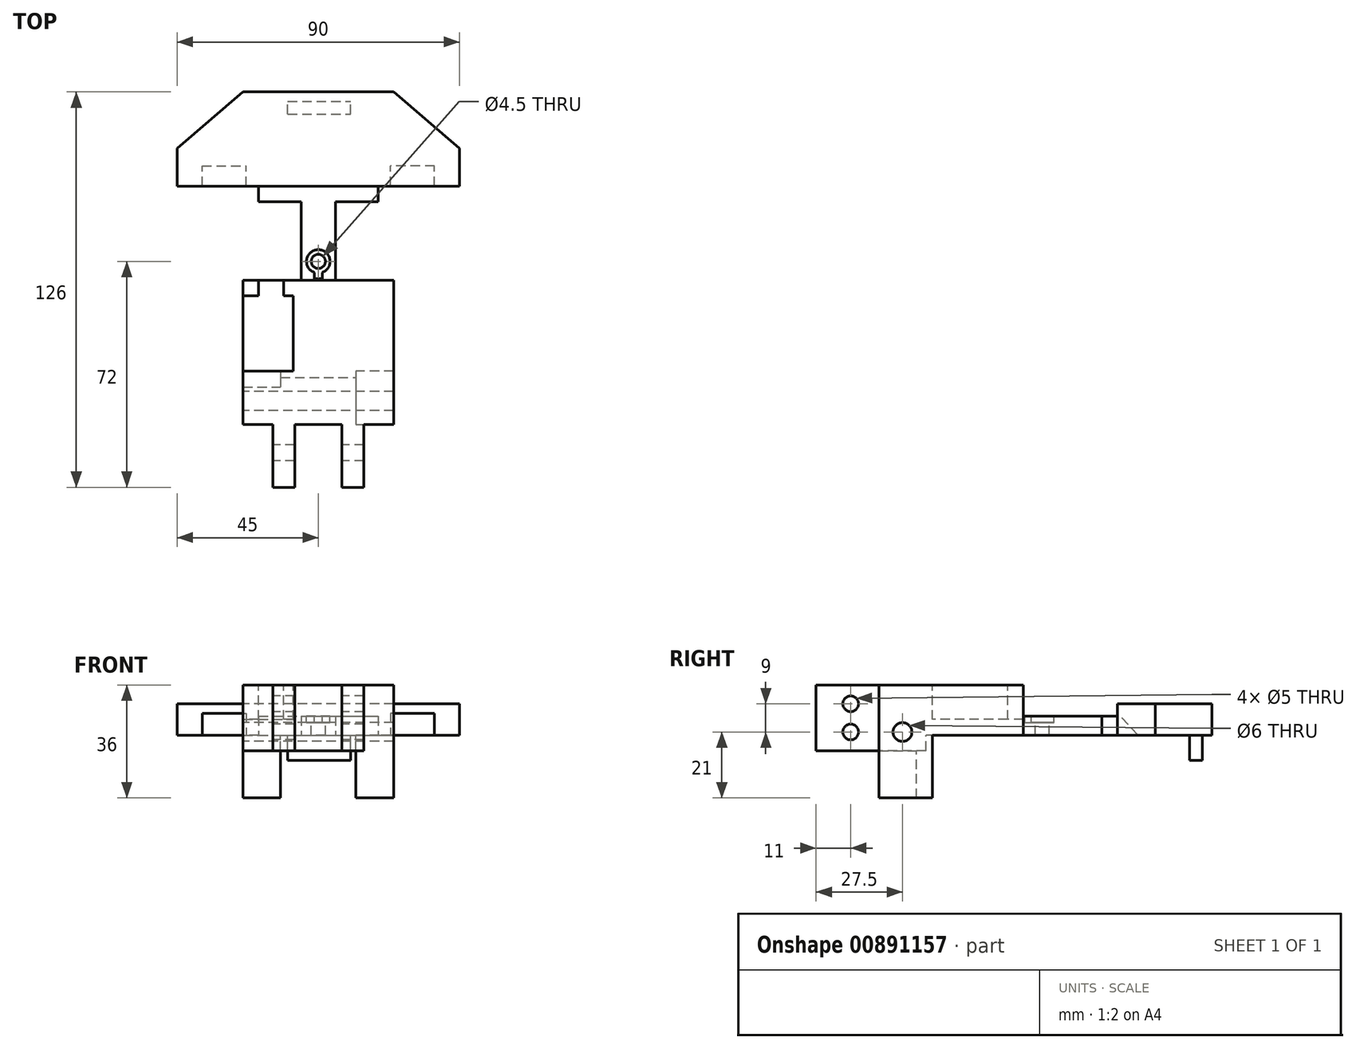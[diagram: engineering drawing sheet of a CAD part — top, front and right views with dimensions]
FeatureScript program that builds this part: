
annotation { "Feature Type Name" : "Feature", "Feature Type Description" : "" }
export const myFeature = defineFeature(function(context is Context, id is Id, definition is map)
    precondition{}
    {
        {
            var Q0;
            Q0=qCreatedBy(makeId("Top.planeOp"),FACE);
            var sketch = newSketch(context, id + "F0", { "sketchPlane" : qUnion([Q0])});
            skLineSegment(sketch, "E0.bottom", {"start": v(-24, 0) * mm, "end": v(24, 0) * mm});
            skLineSegment(sketch, "E0.top", {"start": v(-24, -46) * mm, "end": v(24, -46) * mm});
            skLineSegment(sketch, "E0.left", {"start": v(-24, 0) * mm, "end": v(-24, -46) * mm});
            skLineSegment(sketch, "E0.right", {"start": v(24, 0) * mm, "end": v(24, -46) * mm});
            skSolve(sketch);
        }
        {
            var Q0;
            Q0=makeQuery(id+"F0.imprint","IMPRINT",FACE,{"disambiguationData":[TD([[makeQuery(id+"F0.imprint","IMPRINT",EDGE,{"derivedFrom":sQuery(id+"F0.wireOp",EDGE,"E0.bottom")}),-1.0]])]});
            extrude(context, id + "F1", {"entities" : qUnion([Q0]), "depth" : 16 * mm, "offsetDistance" : 25 * mm});
        }
        {
            var Q0;
            Q0=qCreatedBy(makeId("Top.planeOp"),FACE);
            var sketch = newSketch(context, id + "F2", { "sketchPlane" : qUnion([Q0])});
            skLineSegment(sketch, "E1.bottom", {"start": v(-5.5, 0) * mm, "end": v(5.5, 0) * mm});
            skLineSegment(sketch, "E1.top", {"start": v(-5.5, 25) * mm, "end": v(5.5, 25) * mm});
            skLineSegment(sketch, "E1.left", {"start": v(-5.5, 0) * mm, "end": v(-5.5, 25) * mm});
            skLineSegment(sketch, "E1.right", {"start": v(5.5, 0) * mm, "end": v(5.5, 25) * mm});
            skLineSegment(sketch, "E2.bottom", {"start": v(-19, 25) * mm, "end": v(19, 25) * mm});
            skLineSegment(sketch, "E2.top", {"start": v(-19, 30) * mm, "end": v(19, 30) * mm});
            skLineSegment(sketch, "E2.left", {"start": v(-19, 25) * mm, "end": v(-19, 30) * mm});
            skLineSegment(sketch, "E2.right", {"start": v(19, 25) * mm, "end": v(19, 30) * mm});
            skSolve(sketch);
        }
        {
            var Q0;
            Q0=makeQuery(id+"F2.imprint","IMPRINT",FACE,{"disambiguationData":[TD([[makeQuery(id+"F2.imprint","IMPRINT",EDGE,{"derivedFrom":sQuery(id+"F2.wireOp",EDGE,"E1.bottom")}),1.0]])]});
            var Q1;
            Q1=makeQuery(id+"F2.imprint","IMPRINT",FACE,{"disambiguationData":[TD([[makeQuery(id+"F2.imprint","IMPRINT",EDGE,{"derivedFrom":sQuery(id+"F2.wireOp",EDGE,"E2.top")}),-1.0]])]});
            extrude(context, id + "F3", {"entities" : qUnion([Q0, Q1]), "operationType" : NewBodyOperationType.ADD, "depth" : 6 * mm, "offsetDistance" : 25 * mm});
        }
        {
            var Q0;
            Q0=qCreatedBy(makeId("Top.planeOp"),FACE);
            var sketch = newSketch(context, id + "F4", { "sketchPlane" : qUnion([Q0])});
            skLineSegment(sketch, "E3", {"start": v(0, 30) * mm, "end": v(-45, 30) * mm});
            skLineSegment(sketch, "E4", {"start": v(-45, 30) * mm, "end": v(-45, 42) * mm});
            skLineSegment(sketch, "E5", {"start": v(-45, 42) * mm, "end": v(-24, 60) * mm});
            skLineSegment(sketch, "E6", {"start": v(-24, 60) * mm, "end": v(24, 60) * mm});
            skLineSegment(sketch, "E7", {"start": v(24, 60) * mm, "end": v(45, 42) * mm});
            skLineSegment(sketch, "E8", {"start": v(45, 42) * mm, "end": v(45, 30) * mm});
            skLineSegment(sketch, "E9", {"start": v(45, 30) * mm, "end": v(0, 30) * mm});
            skSolve(sketch);
        }
        {
            var Q0;
            Q0=makeQuery(id+"F4.imprint","IMPRINT",FACE,{"disambiguationData":[TD([[makeQuery(id+"F4.imprint","IMPRINT",EDGE,{"derivedFrom":sQuery(id+"F4.wireOp",EDGE,"E3")}),-1.0]])]});
            extrude(context, id + "F5", {"entities" : qUnion([Q0]), "operationType" : NewBodyOperationType.ADD, "depth" : 10 * mm, "offsetDistance" : 25 * mm});
        }
        {
            var Q0;
            Q0=makeQuery(id+"F5.boolean.opBoolean","MERGE",FACE,{"derivedFrom":[makeQuery(id+"F3.boolean.opBoolean","MERGE",FACE,{"derivedFrom":[makeQuery(id+"F1.opExtrude","CAP_FACE",FACE,{"disambiguationData":[OSD([sQuery(id+"F0.wireOp",EDGE,"E0.bottom"),sQuery(id+"F0.wireOp",EDGE,"E0.top"),sQuery(id+"F0.wireOp",EDGE,"E0.left"),sQuery(id+"F0.wireOp",EDGE,"E0.right")])],"isStart":true}),makeQuery(id+"F3.opExtrude","CAP_FACE",FACE,{"disambiguationData":[OSD([sQuery(id+"F2.wireOp",EDGE,"E1.bottom"),sQuery(id+"F2.wireOp",EDGE,"E1.left"),sQuery(id+"F2.wireOp",EDGE,"E1.right"),sQuery(id+"F2.wireOp",EDGE,"E2.bottom"),sQuery(id+"F2.wireOp",EDGE,"E2.top"),sQuery(id+"F2.wireOp",EDGE,"E2.left"),sQuery(id+"F2.wireOp",EDGE,"E2.right")])],"isStart":true})]}),makeQuery(id+"F5.opExtrude","CAP_FACE",FACE,{"disambiguationData":[OSD([sQuery(id+"F4.wireOp",EDGE,"E3"),sQuery(id+"F4.wireOp",EDGE,"E4"),sQuery(id+"F4.wireOp",EDGE,"E5"),sQuery(id+"F4.wireOp",EDGE,"E6"),sQuery(id+"F4.wireOp",EDGE,"E7"),sQuery(id+"F4.wireOp",EDGE,"E8"),sQuery(id+"F4.wireOp",EDGE,"E9")])],"isStart":true})]});
            var sketch = newSketch(context, id + "F6", { "sketchPlane" : qUnion([Q0])});
            skLineSegment(sketch, "E10.bottom", {"start": v(-24, 29) * mm, "end": v(-12, 29) * mm});
            skLineSegment(sketch, "E10.top", {"start": v(-24, 34) * mm, "end": v(-12, 34) * mm});
            skLineSegment(sketch, "E10.left", {"start": v(-24, 29) * mm, "end": v(-24, 34) * mm});
            skLineSegment(sketch, "E10.right", {"start": v(-12, 29) * mm, "end": v(-12, 34) * mm});
            skLineSegment(sketch, "E11.bottom", {"start": v(24, 29) * mm, "end": v(12, 29) * mm});
            skLineSegment(sketch, "E11.top", {"start": v(24, 46) * mm, "end": v(12, 46) * mm});
            skLineSegment(sketch, "E11.left", {"start": v(24, 29) * mm, "end": v(24, 46) * mm});
            skLineSegment(sketch, "E11.right", {"start": v(12, 29) * mm, "end": v(12, 46) * mm});
            skSolve(sketch);
        }
        {
            var Q0;
            Q0 = qSketchRegion(id + "F6", true);
            extrude(context, id + "F7", {"entities" : qUnion([Q0]), "operationType" : NewBodyOperationType.ADD, "depth" : 20 * mm, "offsetDistance" : 25 * mm});
        }
        {
            var Q0;
            Q0=makeQuery(id+"F5.boolean.opBoolean","MERGE",FACE,{"derivedFrom":[makeQuery(id+"F3.boolean.opBoolean","MERGE",FACE,{"derivedFrom":[makeQuery(id+"F1.opExtrude","CAP_FACE",FACE,{"disambiguationData":[OSD([sQuery(id+"F0.wireOp",EDGE,"E0.bottom"),sQuery(id+"F0.wireOp",EDGE,"E0.top"),sQuery(id+"F0.wireOp",EDGE,"E0.left"),sQuery(id+"F0.wireOp",EDGE,"E0.right")])],"isStart":true}),makeQuery(id+"F3.opExtrude","CAP_FACE",FACE,{"disambiguationData":[OSD([sQuery(id+"F2.wireOp",EDGE,"E1.bottom"),sQuery(id+"F2.wireOp",EDGE,"E1.left"),sQuery(id+"F2.wireOp",EDGE,"E1.right"),sQuery(id+"F2.wireOp",EDGE,"E2.bottom"),sQuery(id+"F2.wireOp",EDGE,"E2.top"),sQuery(id+"F2.wireOp",EDGE,"E2.left"),sQuery(id+"F2.wireOp",EDGE,"E2.right")])],"isStart":true})]}),makeQuery(id+"F5.opExtrude","CAP_FACE",FACE,{"disambiguationData":[OSD([sQuery(id+"F4.wireOp",EDGE,"E3"),sQuery(id+"F4.wireOp",EDGE,"E4"),sQuery(id+"F4.wireOp",EDGE,"E5"),sQuery(id+"F4.wireOp",EDGE,"E6"),sQuery(id+"F4.wireOp",EDGE,"E7"),sQuery(id+"F4.wireOp",EDGE,"E8"),sQuery(id+"F4.wireOp",EDGE,"E9")])],"isStart":true})]});
            var sketch = newSketch(context, id + "F8", { "sketchPlane" : qUnion([Q0])});
            skLineSegment(sketch, "E12.bottom", {"start": v(-24, 46) * mm, "end": v(24, 46) * mm});
            skLineSegment(sketch, "E12.top", {"start": v(-24, 31) * mm, "end": v(24, 31) * mm});
            skLineSegment(sketch, "E12.left", {"start": v(-24, 46) * mm, "end": v(-24, 31) * mm});
            skLineSegment(sketch, "E12.right", {"start": v(24, 46) * mm, "end": v(24, 31) * mm});
            skSolve(sketch);
        }
        {
            var Q0;
            Q0 = qSketchRegion(id + "F8", true);
            extrude(context, id + "F9", {"entities" : qUnion([Q0]), "operationType" : NewBodyOperationType.ADD, "depth" : 5 * mm, "offsetDistance" : 25 * mm});
        }
        {
            var Q0;
            Q0=makeQuery(id+"F9.boolean.opBoolean","MERGE",FACE,{"derivedFrom":[makeQuery(id+"F7.boolean.opBoolean","MERGE",FACE,{"derivedFrom":[makeQuery(id+"F1.opExtrude","SWEPT_FACE",FACE,{"disambiguationData":[OSD([sQuery(id+"F0.wireOp",EDGE,"E0.top")])]}),makeQuery(id+"F7.opExtrude","SWEPT_FACE",FACE,{"disambiguationData":[OSD([sQuery(id+"F6.wireOp",EDGE,"E11.top")])]})]}),makeQuery(id+"F9.opExtrude","SWEPT_FACE",FACE,{"disambiguationData":[OSD([sQuery(id+"F8.wireOp",EDGE,"E12.bottom")])]})]});
            var sketch = newSketch(context, id + "F10", { "sketchPlane" : qUnion([Q0])});
            skLineSegment(sketch, "E13.bottom", {"start": v(-14.5, 16) * mm, "end": v(-7.5, 16) * mm});
            skLineSegment(sketch, "E13.top", {"start": v(-14.5, -5) * mm, "end": v(-7.5, -5) * mm});
            skLineSegment(sketch, "E13.left", {"start": v(-14.5, 16) * mm, "end": v(-14.5, -5) * mm});
            skLineSegment(sketch, "E13.right", {"start": v(-7.5, 16) * mm, "end": v(-7.5, -5) * mm});
            skLineSegment(sketch, "E14.bottom", {"start": v(7.5, 16) * mm, "end": v(14.5, 16) * mm});
            skLineSegment(sketch, "E14.top", {"start": v(7.5, -5) * mm, "end": v(14.5, -5) * mm});
            skLineSegment(sketch, "E14.left", {"start": v(7.5, 16) * mm, "end": v(7.5, -5) * mm});
            skLineSegment(sketch, "E14.right", {"start": v(14.5, 16) * mm, "end": v(14.5, -5) * mm});
            skSolve(sketch);
        }
        {
            var Q0;
            Q0 = qSketchRegion(id + "F10", true);
            extrude(context, id + "F11", {"entities" : qUnion([Q0]), "operationType" : NewBodyOperationType.ADD, "depth" : 20 * mm, "offsetDistance" : 25 * mm});
        }
        {
            var Q0;
            Q0=makeQuery(id+"F11.boolean.opBoolean","MERGE",FACE,{"derivedFrom":[makeQuery(id+"F1.opExtrude","CAP_FACE",FACE,{"disambiguationData":[OSD([sQuery(id+"F0.wireOp",EDGE,"E0.bottom"),sQuery(id+"F0.wireOp",EDGE,"E0.top"),sQuery(id+"F0.wireOp",EDGE,"E0.left"),sQuery(id+"F0.wireOp",EDGE,"E0.right")])],"isStart":false}),makeQuery(id+"F11.opExtrude","SWEPT_FACE",FACE,{"disambiguationData":[OSD([sQuery(id+"F10.wireOp",EDGE,"E13.bottom")])]}),makeQuery(id+"F11.opExtrude","SWEPT_FACE",FACE,{"disambiguationData":[OSD([sQuery(id+"F10.wireOp",EDGE,"E14.bottom")])]})]});
            var sketch = newSketch(context, id + "F12", { "sketchPlane" : qUnion([Q0])});
            skLineSegment(sketch, "E15", {"start": v(-19, 0) * mm, "end": v(-19, -5) * mm});
            skLineSegment(sketch, "E16", {"start": v(-19, -5) * mm, "end": v(-24, -5) * mm});
            skLineSegment(sketch, "E17", {"start": v(-24, -5) * mm, "end": v(-24, -29) * mm});
            skLineSegment(sketch, "E18", {"start": v(-24, -29) * mm, "end": v(-8, -29) * mm});
            skLineSegment(sketch, "E19", {"start": v(-8, -29) * mm, "end": v(-8, -5) * mm});
            skLineSegment(sketch, "E20", {"start": v(-8, -5) * mm, "end": v(-11, -5) * mm});
            skLineSegment(sketch, "E21", {"start": v(-11, -5) * mm, "end": v(-11, 0) * mm});
            skLineSegment(sketch, "E22", {"start": v(-11, 0) * mm, "end": v(-19, 0) * mm});
            skSolve(sketch);
        }
        {
            var Q0;
            Q0=makeQuery(id+"F12.imprint","IMPRINT",FACE,{"disambiguationData":[TD([[makeQuery(id+"F12.imprint","IMPRINT",EDGE,{"derivedFrom":sQuery(id+"F12.wireOp",EDGE,"E15")}),1.0]])]});
            extrude(context, id + "F13", {"entities" : qUnion([Q0]), "operationType" : NewBodyOperationType.REMOVE, "oppositeDirection" : true, "depth" : 11 * mm, "offsetDistance" : 25 * mm});
        }
        {
            var Q0;
            Q0=makeQuery(id+"F11.opExtrude","SWEPT_FACE",FACE,{"disambiguationData":[OSD([sQuery(id+"F10.wireOp",EDGE,"E13.left")])]});
            var sketch = newSketch(context, id + "F14", { "sketchPlane" : qUnion([Q0])});
            skCircle(sketch, "E23", {"center": v(55, 10) * mm, "radius": 2.5 * mm});
            skCircle(sketch, "E24", {"center": v(55, 1) * mm, "radius": 2.5 * mm});
            skSolve(sketch);
        }
        {
            var Q0;
            Q0 = qSketchRegion(id + "F14", true);
            extrude(context, id + "F15", {"entities" : qUnion([Q0]), "operationType" : NewBodyOperationType.REMOVE, "endBound" : BoundingType.THROUGH_ALL, "oppositeDirection" : true, "depth" : 25 * mm, "offsetDistance" : 25 * mm});
        }
        {
            var Q0;
            Q0=makeQuery(id+"F9.boolean.opBoolean","MERGE",FACE,{"derivedFrom":[makeQuery(id+"F7.boolean.opBoolean","MERGE",FACE,{"derivedFrom":[makeQuery(id+"F1.opExtrude","SWEPT_FACE",FACE,{"disambiguationData":[OSD([sQuery(id+"F0.wireOp",EDGE,"E0.left")])]}),makeQuery(id+"F7.opExtrude","SWEPT_FACE",FACE,{"disambiguationData":[OSD([sQuery(id+"F6.wireOp",EDGE,"E10.left")])]})]}),makeQuery(id+"F9.opExtrude","SWEPT_FACE",FACE,{"disambiguationData":[OSD([sQuery(id+"F8.wireOp",EDGE,"E12.left")])]})]});
            var sketch = newSketch(context, id + "F16", { "sketchPlane" : qUnion([Q0])});
            skCircle(sketch, "E25", {"center": v(38.5, 1) * mm, "radius": 3 * mm});
            skSolve(sketch);
        }
        {
            var Q0;
            Q0 = qSketchRegion(id + "F16", true);
            extrude(context, id + "F17", {"entities" : qUnion([Q0]), "operationType" : NewBodyOperationType.REMOVE, "endBound" : BoundingType.THROUGH_ALL, "oppositeDirection" : true, "depth" : 25 * mm, "offsetDistance" : 25 * mm});
        }
        {
            var Q0;
            Q0=makeQuery(id+"F3.opExtrude","CAP_FACE",FACE,{"disambiguationData":[OSD([sQuery(id+"F2.wireOp",EDGE,"E1.bottom"),sQuery(id+"F2.wireOp",EDGE,"E1.left"),sQuery(id+"F2.wireOp",EDGE,"E1.right"),sQuery(id+"F2.wireOp",EDGE,"E2.bottom"),sQuery(id+"F2.wireOp",EDGE,"E2.top"),sQuery(id+"F2.wireOp",EDGE,"E2.left"),sQuery(id+"F2.wireOp",EDGE,"E2.right")])],"isStart":false});
            var sketch = newSketch(context, id + "F18", { "sketchPlane" : qUnion([Q0])});
            skCircle(sketch, "E26", {"center": v(0, 6) * mm, "radius": 2.25 * mm});
            skSolve(sketch);
        }
        {
            var Q0;
            Q0 = qSketchRegion(id + "F18", true);
            extrude(context, id + "F19", {"entities" : qUnion([Q0]), "operationType" : NewBodyOperationType.REMOVE, "endBound" : BoundingType.THROUGH_ALL, "oppositeDirection" : true, "depth" : 25 * mm, "offsetDistance" : 25 * mm});
        }
        {
            var Q0;
            Q0=makeQuery(id+"F3.opExtrude","CAP_FACE",FACE,{"disambiguationData":[OSD([sQuery(id+"F2.wireOp",EDGE,"E1.bottom"),sQuery(id+"F2.wireOp",EDGE,"E1.left"),sQuery(id+"F2.wireOp",EDGE,"E1.right"),sQuery(id+"F2.wireOp",EDGE,"E2.bottom"),sQuery(id+"F2.wireOp",EDGE,"E2.top"),sQuery(id+"F2.wireOp",EDGE,"E2.left"),sQuery(id+"F2.wireOp",EDGE,"E2.right")])],"isStart":false});
            var sketch = newSketch(context, id + "F20", { "sketchPlane" : qUnion([Q0])});
            skArc(sketch, "E27", {"start": v(1.25, 2.46) * mm, "mid": v(0, 9.75) * mm, "end": v(-1.25, 2.46) * mm});
            skLineSegment(sketch, "E28", {"start": v(-1.25, 2.46) * mm, "end": v(-1.25, 0.46) * mm});
            skLineSegment(sketch, "E29", {"start": v(-1.25, 0.46) * mm, "end": v(1.25, 0.46) * mm});
            skLineSegment(sketch, "E30", {"start": v(1.25, 0.46) * mm, "end": v(1.25, 2.46) * mm});
            skSolve(sketch);
        }
        {
            var Q0;
            Q0 = qSketchRegion(id + "F20", true);
            extrude(context, id + "F21", {"entities" : qUnion([Q0]), "operationType" : NewBodyOperationType.REMOVE, "oppositeDirection" : true, "depth" : 2 * mm, "offsetDistance" : 25 * mm});
        }
        {
            var Q0;
            Q0=qCreatedBy(makeId("Right.planeOp"),FACE);
            cPlane(context, id + "F22", {"entities" : qUnion([Q0]), "cplaneType" : CPlaneType.OFFSET, "offset" : 23 * mm, "width" : 150 * mm, "height" : 150 * mm});
        }
        {
            var Q0;
            Q0=qCreatedBy(id+"F22.planeOp",FACE);
            var sketch = newSketch(context, id + "F23", { "sketchPlane" : qUnion([Q0])});
            skLineSegment(sketch, "E31", {"start": v(36.5, 0) * mm, "end": v(30, 7) * mm});
            skLineSegment(sketch, "E32", {"start": v(30, 7) * mm, "end": v(30, 0) * mm});
            skLineSegment(sketch, "E33", {"start": v(30, 0) * mm, "end": v(36.5, 0) * mm});
            skSolve(sketch);
        }
        {
            var Q0;
            Q0 = qSketchRegion(id + "F23", true);
            extrude(context, id + "F24", {"entities" : qUnion([Q0]), "operationType" : NewBodyOperationType.REMOVE, "depth" : 14 * mm, "offsetDistance" : 25 * mm});
        }
        {
            var Q0;
            Q0=qCreatedBy(makeId("Right.planeOp"),FACE);
            cPlane(context, id + "F25", {"entities" : qUnion([Q0]), "cplaneType" : CPlaneType.OFFSET, "offset" : 23 * mm, "oppositeDirection" : true, "width" : 150 * mm, "height" : 150 * mm});
        }
        {
            var Q0;
            Q0=qCreatedBy(id+"F25.planeOp",FACE);
            var sketch = newSketch(context, id + "F26", { "sketchPlane" : qUnion([Q0])});
            skLineSegment(sketch, "E34", {"start": v(36.5, 0) * mm, "end": v(30, 7) * mm});
            skLineSegment(sketch, "E35", {"start": v(30, 7) * mm, "end": v(30, 0) * mm});
            skLineSegment(sketch, "E36", {"start": v(30, 0) * mm, "end": v(36.5, 0) * mm});
            skSolve(sketch);
        }
        {
            var Q0;
            Q0 = qSketchRegion(id + "F26", true);
            extrude(context, id + "F27", {"entities" : qUnion([Q0]), "operationType" : NewBodyOperationType.REMOVE, "oppositeDirection" : true, "depth" : 14 * mm, "offsetDistance" : 25 * mm});
        }
        {
            var Q0;
            {var subQ5=sQuery(id+"F2.wireOp",EDGE,"E1.left");Q0=makeQuery(id+"F8.imprint","IMPRINT",FACE,{"disambiguationData":[TD([[makeQuery(id+"F8.imprint","IMPRINT",EDGE,{"derivedFrom":makeQuery(id+"F3.opExtrude","CAP_EDGE",EDGE,{"disambiguationData":[OSD([subQ5])],"isStart":true})}),1.0]])]});}
            var sketch = newSketch(context, id + "F28", { "sketchPlane" : qUnion([Q0])});
            skLineSegment(sketch, "E37.bottom", {"start": v(-9.72, -53) * mm, "end": v(10.28, -53) * mm});
            skLineSegment(sketch, "E37.top", {"start": v(-9.72, -57) * mm, "end": v(10.28, -57) * mm});
            skLineSegment(sketch, "E37.left", {"start": v(-9.72, -53) * mm, "end": v(-9.72, -57) * mm});
            skLineSegment(sketch, "E37.right", {"start": v(10.28, -53) * mm, "end": v(10.28, -57) * mm});
            skSolve(sketch);
        }
        {
            var Q0;
            Q0 = qSketchRegion(id + "F28", true);
            extrude(context, id + "F29", {"entities" : qUnion([Q0]), "operationType" : NewBodyOperationType.ADD, "depth" : 8 * mm, "offsetDistance" : 25 * mm});
        }
    });
